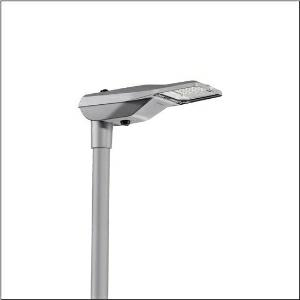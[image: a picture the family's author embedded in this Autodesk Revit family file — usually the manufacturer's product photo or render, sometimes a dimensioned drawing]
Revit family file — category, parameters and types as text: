
# Revit family: streetlight_sl_21_iq_micro___st1_0a_5xe1d31y08db_0307
name_source: partatom
category: Lighting Fixtures
units: mm (PartAtom-declared; Revit-internal decimal feet)

## family parameters
Cut with Voids When Loaded = No
Host = Face
Light Source = No
Part Type = Normal
Room Calculation Point = No
Round Connector Dimension = Use Diameter
Shared = No

## types (1)
- --- (1 x LED, 5110 lm, 39.1 W, 3000K)
    Apparent Load = 39 VA
    CIE Flux Codes = 37 72 97 100 100
    Color Rendering = 70
    Color Temperature = 3000K
    Default Elevation = 1800 mm
    Description = Streetlight SL 21 iQ micro, mast luminaire, primary light control with lens, of PMMA, primary optical cover: cover, of toughened safety glass, transparent, light distribution: ST1.0a, light emission: direct distribution, primary light characteristic: asymmetric, installation type: post-top, side-entry, LED, High Power LED, rated luminous flux: 5.110lm, luminous efficacy: 131lm/W, light colour: 730, colour temperature: 3000K, control gear: iQ-Street Remote, D4i with power reduction, control: pre-setting: logarithmic dimming characteristic, Street-Remote, Auto-Match, Temp-Guard, Lumen-Switch, Night-Set, Smart-Wire, Light-Fading, Desk-Remote (wireless, voltage-free reading and setting of iQ features in the workshop via application-optimized NFC function/RFID function), optimised constant luminous flux control (CLO 2.0), mains connection: 220..240V, AC, 50/60Hz, start of lifetime: 39W, end of service life: 41W, reduction: 17W, luminaire housing, of diecast aluminium, powder-coated, Siteco® metallic grey (DB 702S), corrosivity category C5 mid according to DIN EN ISO 12944, please order mast flange separately, inclination adjustable: 0°, 5°, 10°, 15°, sealing non-destructively replaceable, multi-level sealing system, length: 528mm, width: 235mm, height: 110mm, mast flange for spigot size: 42mm (side-entry): 5XC10008XM4, 60/48mm (side-entry/post-top): 5XC10108XM2, 76/60mm (side-entry/post-top): 5XC10108XM1, mounting height: 4..8m, Smart Interface below and above, protection rating (complete): IP66, insulation class (complete): insulation class II (safety insulation), certification: CE, ENEC, ENEC+, VDE, impact resistance: IK10, permissible operating ambient temperature for outdoor applications: -40..+50°C, standard-compliant lighting for roads and squares, packaging unit: 1 piece

Light Distribution: ST1.0a
    Height = 110 mm
    Lamp = 1 x LED
    Lamp Light Flux = 5110 lm
    Lamp Power = 39.1 W
    Lamp count = 1
    Length = 528 mm
    Luminous efficacy = 131 lm/W
    Manufacturer = Siteco
    ModVariant = No
    Model = 5XE1D31Y08DB
    Number of Poles = 1
    OnlyDefault = Yes
    Power Factor = 1
    Product Name = Streetlight SL 21 iQ micro | ST1.0a
    Product group = mast luminaire | pylon top
    ProductGroupID = 6100
    Protection Class = Protection class II
    Protection Degree = IP 66
    RLX_Detail_Level = 1
    RLX_Emergency_Light_Flux = 0 lm
    RLX_Emergency_Type = 0
    RLX_Emergency_Type_DB = No
    RlxData = <blob elided: 98409 chars, md5=e362d805>
    Socket = socket
    Standby Power = 0 W
    System Light Flux = 5110 lm
    System Power = 39 W
    Type Comments = factory setting: luminous flux: 100 % | dim-lin: 254 | 765 mA
    Type Image = l_1007239.jpg
    URL = http://relux.com
    VarID = @adj_136895
    Voltage = 0 V
    Weight = 0.00 kg
    Width = 235 mm

## geometry (parser evidence)
native form markers: Blend x4, Sweep x11
no freeform markers — native parametric forms only
